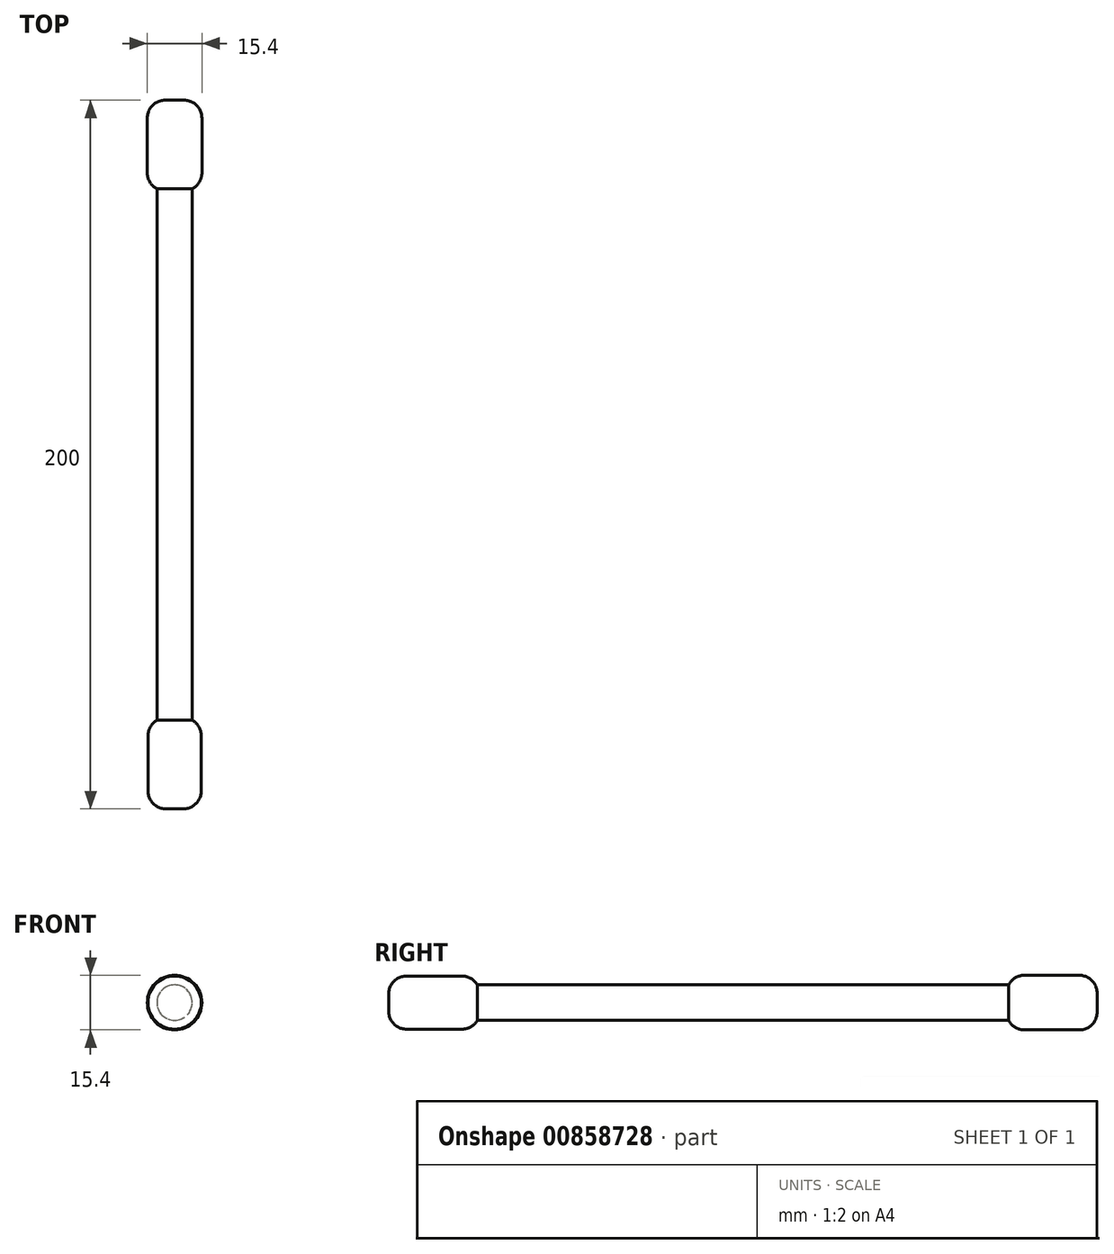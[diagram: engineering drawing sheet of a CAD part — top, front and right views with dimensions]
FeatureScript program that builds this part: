
annotation { "Feature Type Name" : "Feature", "Feature Type Description" : "" }
export const myFeature = defineFeature(function(context is Context, id is Id, definition is map)
    precondition{}
    {
        {
            var Q0;
            Q0=qCreatedBy(makeId("Front.planeOp"),FACE);
            var sketch = newSketch(context, id + "F0", { "sketchPlane" : qUnion([Q0])});
            skCircle(sketch, "E0", {"center": v(0, 0) * mm, "radius": 7.5 * mm});
            skCircle(sketch, "E1", {"center": v(0, 0) * mm, "radius": 5 * mm});
            skSolve(sketch);
        }
        {
            var Q0;
            Q0=makeQuery(id+"F0.imprint","IMPRINT",FACE,{"disambiguationData":[TD([[makeQuery(id+"F0.imprint","IMPRINT",EDGE,{"derivedFrom":sQuery(id+"F0.wireOp",EDGE,"E1")}),1.0]])]});
            extrude(context, id + "F1", {"entities" : qUnion([Q0]), "oppositeDirection" : true, "depth" : 150 * mm, "offsetDistance" : 25 * mm});
        }
        {
            var Q0;
            Q0=makeQuery(id+"F1.opExtrude","CAP_FACE",FACE,{"disambiguationData":[OSD([sQuery(id+"F0.wireOp",EDGE,"E1")])],"isStart":true});
            var Q1;
            Q1=makeQuery(id+"F0.imprint","IMPRINT",FACE,{"disambiguationData":[TD([[makeQuery(id+"F0.imprint","IMPRINT",EDGE,{"derivedFrom":sQuery(id+"F0.wireOp",EDGE,"E0")}),1.0]])]});
            extrude(context, id + "F2", {"entities" : qUnion([Q0, Q1]), "operationType" : NewBodyOperationType.ADD, "depth" : 25 * mm, "offsetDistance" : 25 * mm});
        }
        {
            var Q0;
            Q0=makeQuery(id+"F1.opExtrude","CAP_FACE",FACE,{"disambiguationData":[OSD([sQuery(id+"F0.wireOp",EDGE,"E1")])],"isStart":false});
            var sketch = newSketch(context, id + "F3", { "sketchPlane" : qUnion([Q0])});
            skPoint(sketch, "E2.center.orphan", {"position": v(150.62, 0) * mm});
            skCircle(sketch, "E3", {"center": v(0, 0) * mm, "radius": 7.7 * mm});
            skSolve(sketch);
        }
        {
            var Q0;
            Q0=makeQuery(id+"F3.imprint","IMPRINT",FACE,{"disambiguationData":[TD([[makeQuery(id+"F3.imprint","IMPRINT",EDGE,{"derivedFrom":sQuery(id+"F3.wireOp",EDGE,"E3")}),1.0]])]});
            var Q1;
            Q1=makeQuery(id+"F3.imprint","IMPRINT",FACE,{"disambiguationData":[TD([[makeQuery(id+"F3.imprint","IMPRINT",EDGE,{"derivedFrom":makeQuery(id+"F1.opExtrude","CAP_EDGE",EDGE,{"disambiguationData":[OSD([sQuery(id+"F0.wireOp",EDGE,"E1")])],"isStart":false})}),-1.0]])]});
            extrude(context, id + "F4", {"entities" : qUnion([Q0, Q1]), "operationType" : NewBodyOperationType.ADD, "depth" : 25 * mm, "offsetDistance" : 25 * mm});
        }
        {
            var Q0;
            Q0=makeQuery(id+"F2.opExtrude","CAP_EDGE",EDGE,{"disambiguationData":[OSD([sQuery(id+"F0.wireOp",EDGE,"E0")])],"isStart":false});
            var Q1;
            Q1=makeQuery(id+"F2.opExtrude","CAP_EDGE",EDGE,{"disambiguationData":[OSD([sQuery(id+"F0.wireOp",EDGE,"E0")])],"isStart":true});
            var Q2;
            Q2=makeQuery(id+"F4.opExtrude","CAP_EDGE",EDGE,{"disambiguationData":[OSD([sQuery(id+"F3.wireOp",EDGE,"E3")])],"isStart":false});
            var Q3;
            Q3=makeQuery(id+"F4.opExtrude","CAP_EDGE",EDGE,{"disambiguationData":[OSD([sQuery(id+"F3.wireOp",EDGE,"E3")])],"isStart":true});
            fillet(context, id + "F5", {"entities" : qUnion([Q0, Q1, Q2, Q3]), "radius" : 5 * mm, "tangentPropagation" : true, "allowEdgeOverflow" : false});
        }
    });
